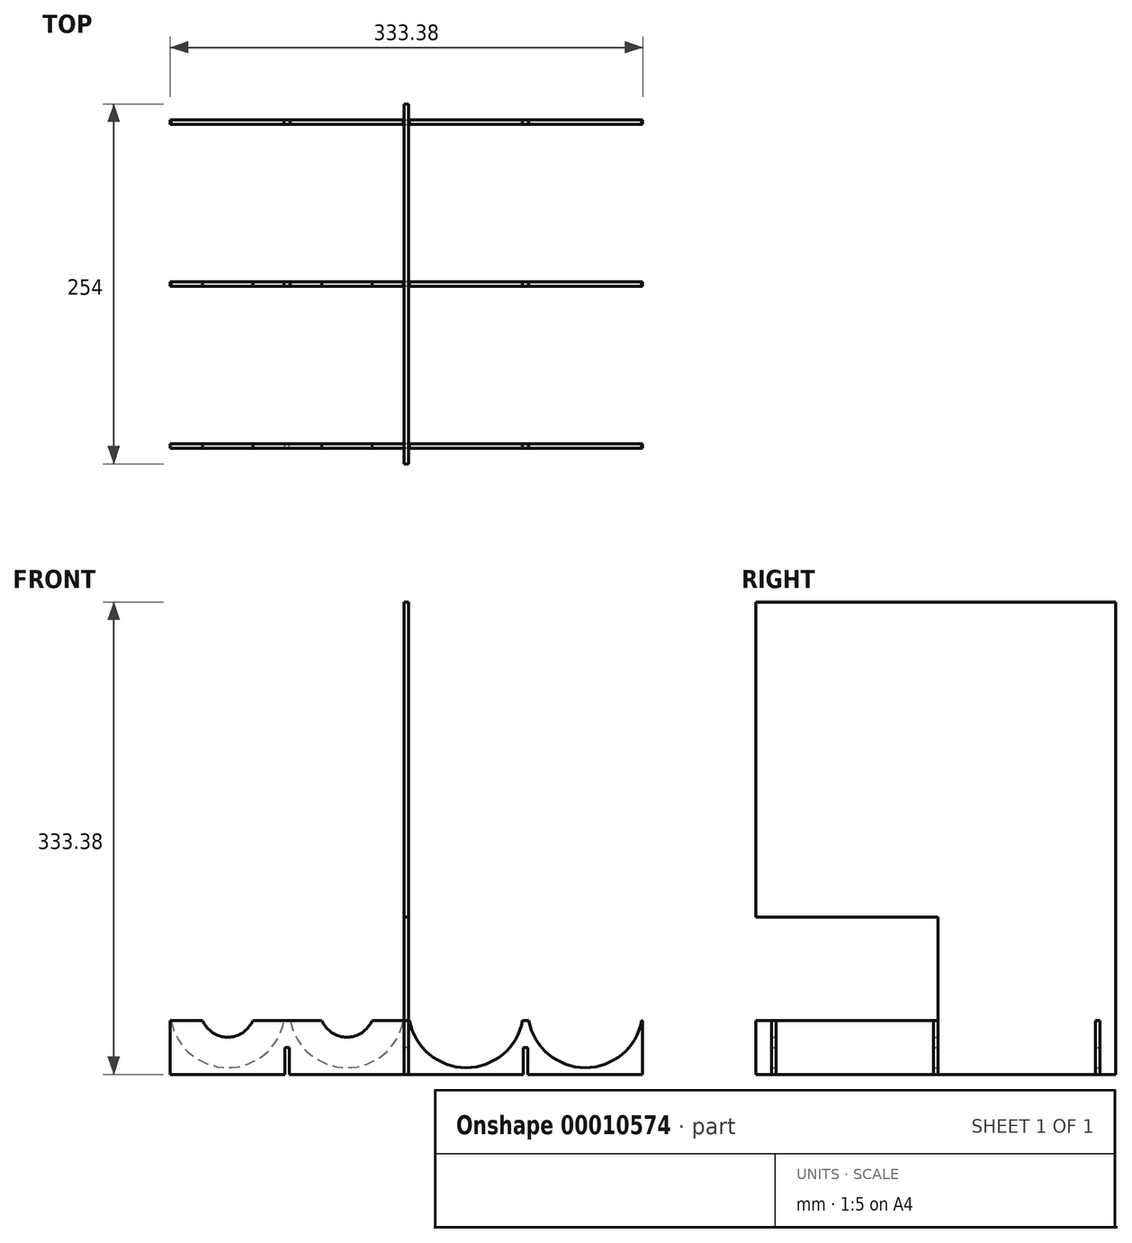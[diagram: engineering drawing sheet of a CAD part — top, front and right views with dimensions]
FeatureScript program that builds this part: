
annotation { "Feature Type Name" : "Feature", "Feature Type Description" : "" }
export const myFeature = defineFeature(function(context is Context, id is Id, definition is map)
    precondition{}
    {
        {
            var Q0;
            Q0=qCreatedBy(makeId("Front.planeOp"),FACE);
            var sketch = newSketch(context, id + "F0", { "sketchPlane" : qUnion([Q0])});
            skLineSegment(sketch, "E0.bottom", {"start": v(-166.69, 0) * mm, "end": v(166.69, 0) * mm, "construction": true});
            skLineSegment(sketch, "E0.top", {"start": v(-166.69, 45.24) * mm, "end": v(166.69, 45.24) * mm, "construction": true});
            skLineSegment(sketch, "E0.left", {"start": v(-166.69, 0) * mm, "end": v(-166.69, 45.24) * mm, "construction": true});
            skLineSegment(sketch, "E0.right", {"start": v(166.69, 0) * mm, "end": v(166.69, 45.24) * mm, "construction": true});
            skCircle(sketch, "E1", {"center": v(-126.2, 45.24) * mm, "radius": 40.48 * mm});
            skCircle(sketch, "E2", {"center": v(-42.07, 45.24) * mm, "radius": 40.48 * mm});
            skCircle(sketch, "E3.0.MirrorC", {"center": v(42.07, 45.24) * mm, "radius": 40.48 * mm});
            skCircle(sketch, "E3.1.MirrorC", {"center": v(126.2, 45.24) * mm, "radius": 40.48 * mm});
            skLineSegment(sketch, "E4.bottom", {"start": v(-166.69, 0) * mm, "end": v(166.69, 0) * mm});
            skLineSegment(sketch, "E4.top", {"start": v(-166.69, 38.1) * mm, "end": v(166.69, 38.1) * mm});
            skLineSegment(sketch, "E4.left", {"start": v(-166.69, 0) * mm, "end": v(-166.69, 38.1) * mm});
            skLineSegment(sketch, "E4.right", {"start": v(166.69, 0) * mm, "end": v(166.69, 38.1) * mm});
            skLineSegment(sketch, "E5.bottom", {"start": v(-85.73, 45.24) * mm, "end": v(-82.55, 45.24) * mm, "construction": true});
            skLineSegment(sketch, "E5.top", {"start": v(-85.73, 0) * mm, "end": v(-82.55, 0) * mm, "construction": true});
            skLineSegment(sketch, "E5.left", {"start": v(-85.73, 45.24) * mm, "end": v(-85.73, 0) * mm, "construction": true});
            skLineSegment(sketch, "E5.right", {"start": v(-82.55, 45.24) * mm, "end": v(-82.55, 0) * mm, "construction": true});
            skLineSegment(sketch, "E6.bottom", {"start": v(-1.59, 45.24) * mm, "end": v(1.59, 45.24) * mm, "construction": true});
            skLineSegment(sketch, "E6.top", {"start": v(-1.59, 0) * mm, "end": v(1.59, 0) * mm, "construction": true});
            skLineSegment(sketch, "E6.left", {"start": v(-1.59, 45.24) * mm, "end": v(-1.59, 0) * mm, "construction": true});
            skLineSegment(sketch, "E6.right", {"start": v(1.59, 45.24) * mm, "end": v(1.59, 0) * mm, "construction": true});
            skLineSegment(sketch, "E7.bottom", {"start": v(82.55, 45.24) * mm, "end": v(85.73, 45.24) * mm, "construction": true});
            skLineSegment(sketch, "E7.top", {"start": v(82.55, 0) * mm, "end": v(85.73, 0) * mm, "construction": true});
            skLineSegment(sketch, "E7.left", {"start": v(82.55, 45.24) * mm, "end": v(82.55, 0) * mm, "construction": true});
            skLineSegment(sketch, "E7.right", {"start": v(85.73, 45.24) * mm, "end": v(85.73, 0) * mm, "construction": true});
            skLineSegment(sketch, "E8.bottom", {"start": v(-85.73, 0) * mm, "end": v(-82.55, 0) * mm});
            skLineSegment(sketch, "E8.top", {"start": v(-85.73, 19.05) * mm, "end": v(-82.55, 19.05) * mm});
            skLineSegment(sketch, "E8.left", {"start": v(-85.73, 0) * mm, "end": v(-85.73, 19.05) * mm});
            skLineSegment(sketch, "E8.right", {"start": v(-82.55, 0) * mm, "end": v(-82.55, 19.05) * mm});
            skLineSegment(sketch, "E9.bottom", {"start": v(-1.59, 0) * mm, "end": v(1.59, 0) * mm});
            skLineSegment(sketch, "E9.top", {"start": v(-1.59, 19.05) * mm, "end": v(1.59, 19.05) * mm});
            skLineSegment(sketch, "E9.left", {"start": v(-1.59, 0) * mm, "end": v(-1.59, 19.05) * mm});
            skLineSegment(sketch, "E9.right", {"start": v(1.59, 0) * mm, "end": v(1.59, 19.05) * mm});
            skLineSegment(sketch, "E10.bottom", {"start": v(82.55, 0) * mm, "end": v(85.73, 0) * mm});
            skLineSegment(sketch, "E10.top", {"start": v(82.55, 19.05) * mm, "end": v(85.73, 19.05) * mm});
            skLineSegment(sketch, "E10.left", {"start": v(82.55, 0) * mm, "end": v(82.55, 19.05) * mm});
            skLineSegment(sketch, "E10.right", {"start": v(85.73, 0) * mm, "end": v(85.73, 19.05) * mm});
            skCircle(sketch, "E11", {"center": v(-126.2, 45.24) * mm, "radius": 19.05 * mm});
            skCircle(sketch, "E12", {"center": v(-42.07, 45.24) * mm, "radius": 19.05 * mm});
            skCircle(sketch, "E13.0.MirrorC", {"center": v(42.07, 45.24) * mm, "radius": 19.05 * mm});
            skCircle(sketch, "E13.1.MirrorC", {"center": v(126.2, 45.24) * mm, "radius": 19.05 * mm});
            skSolve(sketch);
        }
        {
            var Q0;
            {var subQ15=sQuery(id+"F0.wireOp",EDGE,"E4.left");Q0=makeQuery(id+"F0.imprint","IMPRINT",FACE,{"disambiguationData":[TD([[makeQuery(id+"F0.imprint","IMPRINT",EDGE,{"derivedFrom":subQ15}),-1.0]])]});}
            extrude(context, id + "F1", {"entities" : qUnion([Q0]), "endBound" : BoundingType.SYMMETRIC, "depth" : 3.17 * mm});
        }
        {
            var Q0;
            Q0=makeQuery(id+"F1.opExtrude","SWEPT_BODY",BODY,{"disambiguationData":[OSD([sQuery(id+"F0.wireOp",EDGE,"E1"),sQuery(id+"F0.wireOp",EDGE,"E2"),sQuery(id+"F0.wireOp",EDGE,"E3.0.MirrorC"),sQuery(id+"F0.wireOp",EDGE,"E3.1.MirrorC"),sQuery(id+"F0.wireOp",EDGE,"E4.bottom"),sQuery(id+"F0.wireOp",EDGE,"E4.top"),sQuery(id+"F0.wireOp",EDGE,"E4.left"),sQuery(id+"F0.wireOp",EDGE,"E4.right"),sQuery(id+"F0.wireOp",EDGE,"E8.top"),sQuery(id+"F0.wireOp",EDGE,"E8.left"),sQuery(id+"F0.wireOp",EDGE,"E8.right"),sQuery(id+"F0.wireOp",EDGE,"E9.top"),sQuery(id+"F0.wireOp",EDGE,"E9.left"),sQuery(id+"F0.wireOp",EDGE,"E9.right"),sQuery(id+"F0.wireOp",EDGE,"E10.top"),sQuery(id+"F0.wireOp",EDGE,"E10.left"),sQuery(id+"F0.wireOp",EDGE,"E10.right")])]});
            transform(context, id + "F2", {"entities" : qUnion([Q0]), "transformType" : TransformType.TRANSLATION_3D, "dx" : 0 * mm, "dy" : 114.3 * mm, "dz" : 0 * mm, "makeCopy" : true});
        }
        {
            var Q0;
            {var subQ15=sQuery(id+"F0.wireOp",EDGE,"E4.left");Q0=makeQuery(id+"F0.imprint","IMPRINT",FACE,{"disambiguationData":[TD([[makeQuery(id+"F0.imprint","IMPRINT",EDGE,{"derivedFrom":subQ15}),-1.0]])]});}
            var Q1;
            {var subQ1=sQuery(id+"F0.wireOp",EDGE,"E4.top");var subQ4=sQuery(id+"F0.wireOp",EDGE,"E1");var subQ6=makeQuery(id+"F0.imprint","INTERSECT",VERTEX,{"disambiguationData":[OD(0.0)],"derivedFrom":[subQ4,subQ1]});Q1=makeQuery(id+"F0.imprint","IMPRINT",FACE,{"disambiguationData":[TD([[makeQuery(id+"F0.imprint","IMPRINT",EDGE,{"disambiguationData":[TD([[subQ6,-1.0]])],"derivedFrom":subQ4}),1.0]])]});}
            var Q2;
            {var subQ1=sQuery(id+"F0.wireOp",EDGE,"E4.top");var subQ4=sQuery(id+"F0.wireOp",EDGE,"E2");var subQ6=makeQuery(id+"F0.imprint","INTERSECT",VERTEX,{"disambiguationData":[OD(0.0)],"derivedFrom":[subQ4,subQ1]});Q2=makeQuery(id+"F0.imprint","IMPRINT",FACE,{"disambiguationData":[TD([[makeQuery(id+"F0.imprint","IMPRINT",EDGE,{"disambiguationData":[TD([[subQ6,-1.0]])],"derivedFrom":subQ4}),1.0]])]});}
            var Q3;
            {var subQ1=sQuery(id+"F0.wireOp",EDGE,"E4.top");var subQ4=sQuery(id+"F0.wireOp",EDGE,"E3.0.MirrorC");var subQ6=makeQuery(id+"F0.imprint","INTERSECT",VERTEX,{"disambiguationData":[OD(0.0)],"derivedFrom":[subQ4,subQ1]});Q3=makeQuery(id+"F0.imprint","IMPRINT",FACE,{"disambiguationData":[TD([[makeQuery(id+"F0.imprint","IMPRINT",EDGE,{"disambiguationData":[TD([[subQ6,1.0]])],"derivedFrom":subQ4}),-1.0]])]});}
            var Q4;
            {var subQ1=sQuery(id+"F0.wireOp",EDGE,"E4.top");var subQ4=sQuery(id+"F0.wireOp",EDGE,"E3.1.MirrorC");var subQ6=makeQuery(id+"F0.imprint","INTERSECT",VERTEX,{"disambiguationData":[OD(0.0)],"derivedFrom":[subQ4,subQ1]});Q4=makeQuery(id+"F0.imprint","IMPRINT",FACE,{"disambiguationData":[TD([[makeQuery(id+"F0.imprint","IMPRINT",EDGE,{"disambiguationData":[TD([[subQ6,1.0]])],"derivedFrom":subQ4}),-1.0]])]});}
            extrude(context, id + "F3", {"entities" : qUnion([Q0, Q1, Q2, Q3, Q4]), "endBound" : BoundingType.SYMMETRIC, "depth" : 3.17 * mm});
        }
        {
            var Q0;
            Q0=makeQuery(id+"F3.opExtrude","SWEPT_BODY",BODY,{"disambiguationData":[OSD([sQuery(id+"F0.wireOp",EDGE,"E4.bottom"),sQuery(id+"F0.wireOp",EDGE,"E4.top"),sQuery(id+"F0.wireOp",EDGE,"E4.left"),sQuery(id+"F0.wireOp",EDGE,"E4.right"),sQuery(id+"F0.wireOp",EDGE,"E8.top"),sQuery(id+"F0.wireOp",EDGE,"E8.left"),sQuery(id+"F0.wireOp",EDGE,"E8.right"),sQuery(id+"F0.wireOp",EDGE,"E9.top"),sQuery(id+"F0.wireOp",EDGE,"E9.left"),sQuery(id+"F0.wireOp",EDGE,"E9.right"),sQuery(id+"F0.wireOp",EDGE,"E10.top"),sQuery(id+"F0.wireOp",EDGE,"E10.left"),sQuery(id+"F0.wireOp",EDGE,"E10.right"),sQuery(id+"F0.wireOp",EDGE,"E11"),sQuery(id+"F0.wireOp",EDGE,"E12"),sQuery(id+"F0.wireOp",EDGE,"E13.0.MirrorC"),sQuery(id+"F0.wireOp",EDGE,"E13.1.MirrorC")])]});
            transform(context, id + "F4", {"entities" : qUnion([Q0]), "transformType" : TransformType.TRANSLATION_3D, "dx" : 0 * mm, "dy" : -114.3 * mm, "dz" : 0 * mm, "makeCopy" : true});
        }
        {
            var Q0;
            Q0=qCreatedBy(makeId("Right.planeOp"),FACE);
            var sketch = newSketch(context, id + "F5", { "sketchPlane" : qUnion([Q0])});
            skLineSegment(sketch, "E14.bottom", {"start": v(-127, 333.38) * mm, "end": v(127, 333.38) * mm});
            skLineSegment(sketch, "E14.top", {"start": v(-127, 0) * mm, "end": v(127, 0) * mm});
            skLineSegment(sketch, "E14.left", {"start": v(-127, 333.37) * mm, "end": v(-127, 0) * mm});
            skLineSegment(sketch, "E14.right", {"start": v(127, 333.37) * mm, "end": v(127, 0) * mm});
            skLineSegment(sketch, "E15", {"start": v(-127, 111.12) * mm, "end": v(127, 111.12) * mm, "construction": true});
            skLineSegment(sketch, "E16", {"start": v(-127, 38.1) * mm, "end": v(-115.89, 38.1) * mm});
            skLineSegment(sketch, "E17", {"start": v(-115.89, 38.1) * mm, "end": v(-115.89, 19.05) * mm});
            skLineSegment(sketch, "E18", {"start": v(-115.89, 19.05) * mm, "end": v(-112.71, 19.05) * mm});
            skLineSegment(sketch, "E19", {"start": v(-112.71, 19.05) * mm, "end": v(-112.71, 38.1) * mm});
            skLineSegment(sketch, "E20", {"start": v(-112.71, 38.1) * mm, "end": v(-1.59, 38.1) * mm});
            skLineSegment(sketch, "E21", {"start": v(-1.59, 38.1) * mm, "end": v(-1.59, 19.05) * mm});
            skLineSegment(sketch, "E22", {"start": v(-1.59, 19.05) * mm, "end": v(1.59, 19.05) * mm});
            skLineSegment(sketch, "E23", {"start": v(1.59, 19.05) * mm, "end": v(1.59, 111.12) * mm});
            skLineSegment(sketch, "E24", {"start": v(1.59, 111.12) * mm, "end": v(-127, 111.12) * mm});
            skSolve(sketch);
        }
        {
            var Q0;
            {var subQ4=sQuery(id+"F5.wireOp",EDGE,"E14.bottom");Q0=makeQuery(id+"F5.imprint","IMPRINT",FACE,{"disambiguationData":[TD([[makeQuery(id+"F5.imprint","IMPRINT",EDGE,{"derivedFrom":subQ4}),-1.0]])]});}
            extrude(context, id + "F6", {"entities" : qUnion([Q0]), "endBound" : BoundingType.SYMMETRIC, "depth" : 3.17 * mm});
        }
    });
